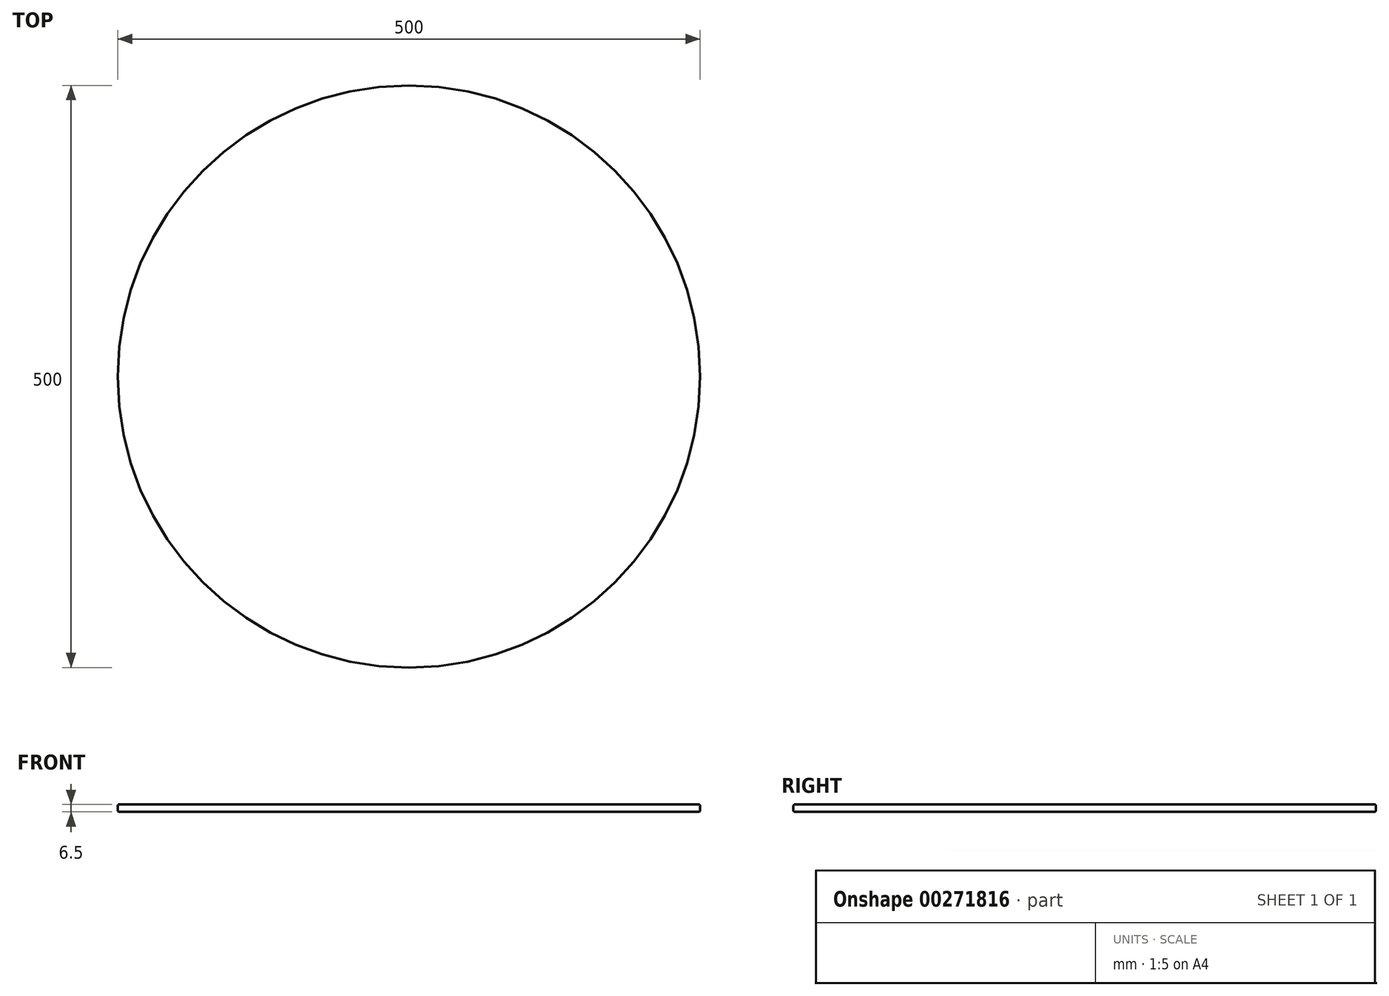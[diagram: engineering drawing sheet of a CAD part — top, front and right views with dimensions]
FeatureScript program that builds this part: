
annotation { "Feature Type Name" : "Feature", "Feature Type Description" : "" }
export const myFeature = defineFeature(function(context is Context, id is Id, definition is map)
    precondition{}
    {
        {
            var Q0;
            Q0=qCreatedBy(makeId("Top.planeOp"),FACE);
            var sketch = newSketch(context, id + "F0", { "sketchPlane" : qUnion([Q0])});
            skCircle(sketch, "E0", {"center": v(0, 0) * mm, "radius": 250 * mm});
            skSolve(sketch);
        }
        {
            var Q0;
            Q0=qSketchRegion(id+"F0",true);
            extrude(context, id + "F1", {"entities" : qUnion([Q0]), "depth" : 6.5 * mm});
        }
        {
            var Q0;
            Q0=makeQuery(id+"F1.opExtrude","CAP_EDGE",EDGE,{"disambiguationData":[OSD([sQuery(id+"F0.wireOp",EDGE,"E0")])],"isStart":false});
            var Q1;
            Q1=makeQuery(id+"F1.opExtrude","CAP_EDGE",EDGE,{"disambiguationData":[OSD([sQuery(id+"F0.wireOp",EDGE,"E0")])],"isStart":true});
            fillet(context, id + "F2", {"entities" : qUnion([Q0, Q1]), "radius" : 1.5 * mm, "tangentPropagation" : true, "allowEdgeOverflow" : false});
        }
    });
